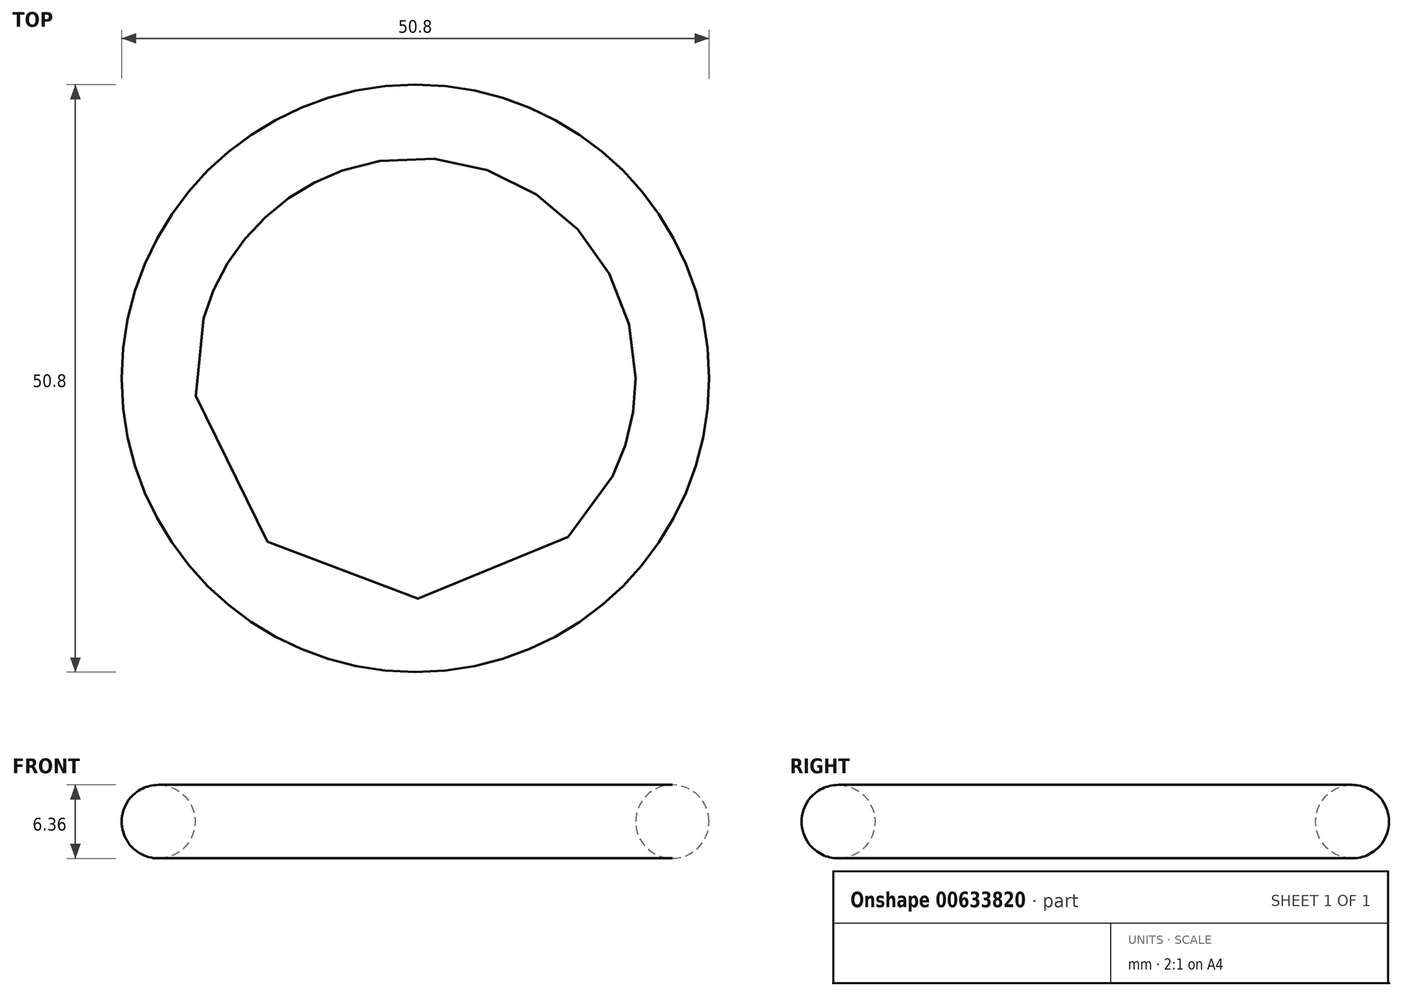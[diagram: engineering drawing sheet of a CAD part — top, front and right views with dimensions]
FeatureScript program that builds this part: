
annotation { "Feature Type Name" : "Feature", "Feature Type Description" : "" }
export const myFeature = defineFeature(function(context is Context, id is Id, definition is map)
    precondition{}
    {
        {
            var Q0;
            Q0=qCreatedBy(makeId("Front.planeOp"),FACE);
            var sketch = newSketch(context, id + "F0", { "sketchPlane" : qUnion([Q0])});
            skCircle(sketch, "E0", {"center": v(-22.23, 0) * mm, "radius": 3.17 * mm});
            skLineSegment(sketch, "E1", {"start": v(0, 10.95) * mm, "end": v(0, -10.6) * mm, "construction": true});
            skSolve(sketch);
        }
        {
            var Q0;
            Q0 = qSketchRegion(id + "F0", true);
            var Q1;
            Q1=sQuery(id+"F0.wireOp",EDGE,"E1");
            revolve(context, id + "F1", {"entities" : qUnion([Q0]), "axis" : qUnion([Q1]), "revolveType" : RevolveType.FULL});
        }
    });
